# Revit family: gdlr200508_MMIDoor-SRP
name_source: partatom
category: Doors
revit_build: Autodesk Revit 2014 (Build: 20130308_1515(x64)
units: mm (PartAtom-declared; Revit-internal decimal feet)

## types (10) — shared parameters
Analytic Construction = Metal
Frame Projection Ext. = 1"
Frame Projection Int. = 1"
Frame Width = 3"
Function = Exterior
Heat Transfer Coefficient (U) = 3.7021 W/(m²·K)
Height = 7' - 0"
Manufacturer = Metal Maufacturing Industries
Thermal Resistance (R) = 0.2701 (m²·K)/W
Thickness = 1 3/4"
URL = http://mmiopenings.com
Wall Closure = By host
Width = 3' - 0"
zero-valued in all types: Solar Heat Gain Coefficient, Visual Light Transmittance

## per-type parameters (varying)
| type | Bottom Cutout | Bottom Glass | Bottom Louver | Description | Full Cutout | Half Cutout | Hardware Set | Model | Narrow Cutout | Top Glass | Top Louver | Vision Cutout |
| F | No | No | No | Flush Pair Door with Single Rabbet Frame | No | No | 01 | SRP-F | No | No | No | No |
| HG | No | No | No | Half Glass Pair Door with Single Rabbet Frame | No | Yes | 06 | SRP-HG | No | Yes | No | No |
| V | No | No | No | Vision Pair Door with Single Rabbet Frame | No | No | 10 | SRP-V | No | Yes | No | Yes |
| NG | No | No | No | Narrow Glass Pair Door with Single Rabbet Frame | No | No | 09 | SRP-NG | Yes | Yes | No | No |
| G2 | Yes | Yes | No | Double Glass Pair Door with Single Rabbet Frame | No | Yes | 04 | SRP-G2 | No | Yes | No | No |
| L2 | Yes | No | Yes | Double Louver Pair Door with Single Rabbet Frame | No | Yes | 08 | SRP-L2 | No | No | Yes | No |
| L | Yes | No | Yes | Louver Pair Door with Single Rabbet Frame | No | No | 07 | SRP-L | No | No | No | No |
| GL | Yes | No | Yes | Glass & Louver Pair Door with Single Rabbet Frame | No | Yes | 05 | SRP-GL | No | Yes | No | No |
| FL | No | No | No | Full Louver Pair Door with Single Rabbet Frame | Yes | No | 03 | SRP-FL | No | No | Yes | No |
| FG | No | No | No | Full Glass Pair Door with Single Rabbet Frame | Yes | No | 02 | SRP-FG | No | Yes | No | No |

## geometry (parser evidence)
native form markers: Sweep x23
no freeform markers — native parametric forms only
